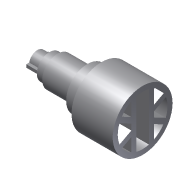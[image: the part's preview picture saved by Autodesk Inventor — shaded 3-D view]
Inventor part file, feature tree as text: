
AUTODESK INVENTOR PART (.ipt)
format: ipt  version: 2012 (Build 160160000, 160)  size: 241,152 bytes
history: native  units: mm
features: sketch x7, extrude x6, revolve x1
ambient origin geometry x8: Origin, YZ Plane, XZ Plane, XY Plane, X Axis, Y Axis, Z Axis, Center Point
bodies: Solid1 (feature_tree)
feature tree (14):
  revolve  "Revolution1"  [1 undecoded]
  extrude  "Extrusion1"  Depth=3.45mm
  extrude  "Extrusion2"  Depth=2.4mm
  extrude  "Extrusion3"  Depth=1.05mm
  extrude  "Extrusion4"  Depth=1.7mm
  extrude  "Extrusion5"  TaperAngle=90.0deg  [1 undecoded]
  extrude  "Extrusion6"  Depth=10.0mm TaperAngle=0.0deg
  sketch  "Sketch1"  dims[d0=11.9mm d1=6.2mm]
  sketch  "Sketch2"  dims[d2=10.2mm d3=3.45mm]
  sketch  "Sketch3"  dims[d4=5.6mm d5=2.4mm]
  sketch  "Sketch4"  dims[d6=11.9mm d7=1.05mm]
  sketch  "Sketch5"  dims[d8=3.2mm d9=1.7mm]
  sketch  "Sketch7"  dims[d10=4.8mm d11=90.0deg]
  sketch  "Sketch8"  dims[d12=2.5mm d13=10.0mm d14=0.0mm d15=23.8mm d16=19.8mm d17=2.0mm d18=2.5mm d19=2.0mm d20=2.0mm d24=2.0mm d25=2.0mm d26=2.0mm d27=2.0mm d28=2.5mm d29=12.0mm d30=0.0mm d32=0.0mm d33=0.0mm d36=5.0mm d37=0.0mm d38=23.0mm d39=0.0mm d40=4.4mm d42=1.2mm d44=1.2mm d46=16.0mm d47=14.0mm d48=0.0mm d49=7.5mm d50=7.5mm d51=14.0mm d52=20.0mm d53=0.0mm]
note: 2 required parameter values undecoded (feature->parameter linkage not recoverable at this tier; creation-order binding heuristic only, values carry confidence <= 0.55)